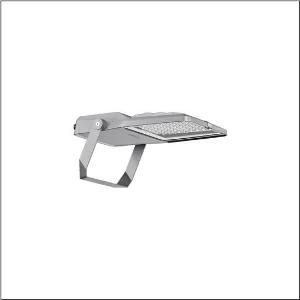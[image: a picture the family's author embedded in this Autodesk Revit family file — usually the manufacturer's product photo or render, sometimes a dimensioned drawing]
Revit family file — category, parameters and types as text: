
# Revit family: floodlight_fl_21_iq_mini___pl43_5xa7771b4a1a_3306
name_source: partatom
category: Lighting Fixtures
units: mm (PartAtom-declared; Revit-internal decimal feet)

## family parameters
Cut with Voids When Loaded = No
Host = Face
Light Source = No
Part Type = Normal
Room Calculation Point = No
Round Connector Dimension = Use Diameter
Shared = No

## types (1)
- --- (1 x LED, 6660 lm, 45.5 W, 4000K)
    Apparent Load = 46 VA
    CIE Flux Codes = 27 78 99 100 100
    Color Rendering = 70
    Color Temperature = 4000K
    Default Elevation = 1800 mm
    Description = Floodlight FL 21 iQ mini, floodlight, primary light control with lens, of PMMA, primary optical cover: protective disc, of toughened safety glass, transparent, light distribution: PL43, light emission: direct distribution, installation type: surface-mounted, LED, High Power LED, rated luminous flux: 6.660lm, luminous efficacy: 146lm/W, light colour: 740, colour temperature: 4000K, control: Auto-Match, Temp-Guard, Lumen-Switch, Night-Set, Smart-Wire, Light-Fading, Desk-Remote (wireless, voltage-free reading and setting of iQ features in the workshop via application-optimized NFC function/RFID function), optimised constant luminous flux control (CLO 2.0), with terminal, 6-pole, mains connection: 220..240V, AC, 50/60Hz, start of lifetime: 46W, end of service life: 48W, reduction: 22W, luminaire housing, of diecast aluminium, powder-coated, Siteco® metallic grey (DB 702S), corrosivity category C5 mid according to DIN EN ISO 12944, sealing non-destructively replaceable, mounting bracket, of steel, galvanised, powder-coated, Siteco® metallic grey (DB 702S), protection rating (complete): IP66, insulation class (complete): insulation class II (safety insulation), certification: CE, ENEC, VDE, protection symbol: D, impact resistance: IK08, permissible operating ambient temperature: -40..+40°C, permissible operating ambient temperature for outdoor applications: -40..+50°C, standard: DIN EN 12944, LABS conformity tested according to VDMA 24364:2018-05, packaging unit: 1 piece

Light Distribution: PL43
    Height = 70 mm
    Lamp = 1 x LED
    Lamp Light Flux = 6660 lm
    Lamp Power = 45.5 W
    Lamp count = 1
    Length = 485 mm
    Luminous efficacy = 146 lm/W
    Manufacturer = Siteco
    ModVariant = No
    Model = 5XA7771B4A1A
    Mounting Place = Wall
    Mounting Type = Surface mounted
    Number of Poles = 1
    OnlyDefault = Yes
    Power Factor = 1
    Product Name = Floodlight FL 21 iQ mini | PL43
    Product group = floodlight | wall mounted
    ProductGroupID = 2001
    Protection Class = Protection class II
    Protection Degree = IP 66
    RLX_Detail_Level = 1
    RLX_Emergency_Light_Flux = 0 lm
    RLX_Emergency_Type = 0
    RLX_Emergency_Type_DB = No
    RlxData = <blob elided: 96177 chars, md5=9cf1cc73>
    Socket = socket
    Standby Power = 0 W
    System Light Flux = 6660 lm
    System Power = 46 W
    Type Comments = factory setting: luminous flux: 100 % | dim-lin: 254 | 463 mA
    Type Image = l_1006845.jpg
    URL = http://relux.com
    VarID = @adj_094313
    Voltage = 0 V
    Weight = 0.00 kg
    Width = 337 mm

## geometry (parser evidence)
native form markers: Blend x4, Sweep x12
no freeform markers — native parametric forms only
